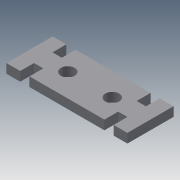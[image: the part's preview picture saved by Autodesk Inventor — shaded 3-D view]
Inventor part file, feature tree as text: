
AUTODESK INVENTOR PART (.ipt)
format: ipt  version: 2013 (Build 170138000, 138)  size: 114,688 bytes
history: native  units: mm
features: extrude x3, sketch x3
ambient origin geometry x8: Origin, YZ Plane, XZ Plane, XY Plane, X Axis, Y Axis, Z Axis, Center Point
bodies: Solid1 (feature_tree)
feature tree (6):
  extrude  "Extrusion1"  Depth=50.0mm
  sketch  "Sketch2"  dims[d2=24.1mm d3=24.1mm]
  extrude  "Extrusion2"  Depth=24.1mm
  extrude  "Extrusion3"  Depth=15.0mm
  sketch  "Sketch1"  dims[d0=131.0mm d1=50.0mm]
  sketch  "Sketch3"  dims[d4=15.0mm d5=15.0mm d6=10.0mm d7=0.0mm d10=15.0mm d12=15.0mm d14=15.0mm d16=15.0mm d18=10.0mm d19=0.0mm d20=10.0mm d21=0.0mm]
